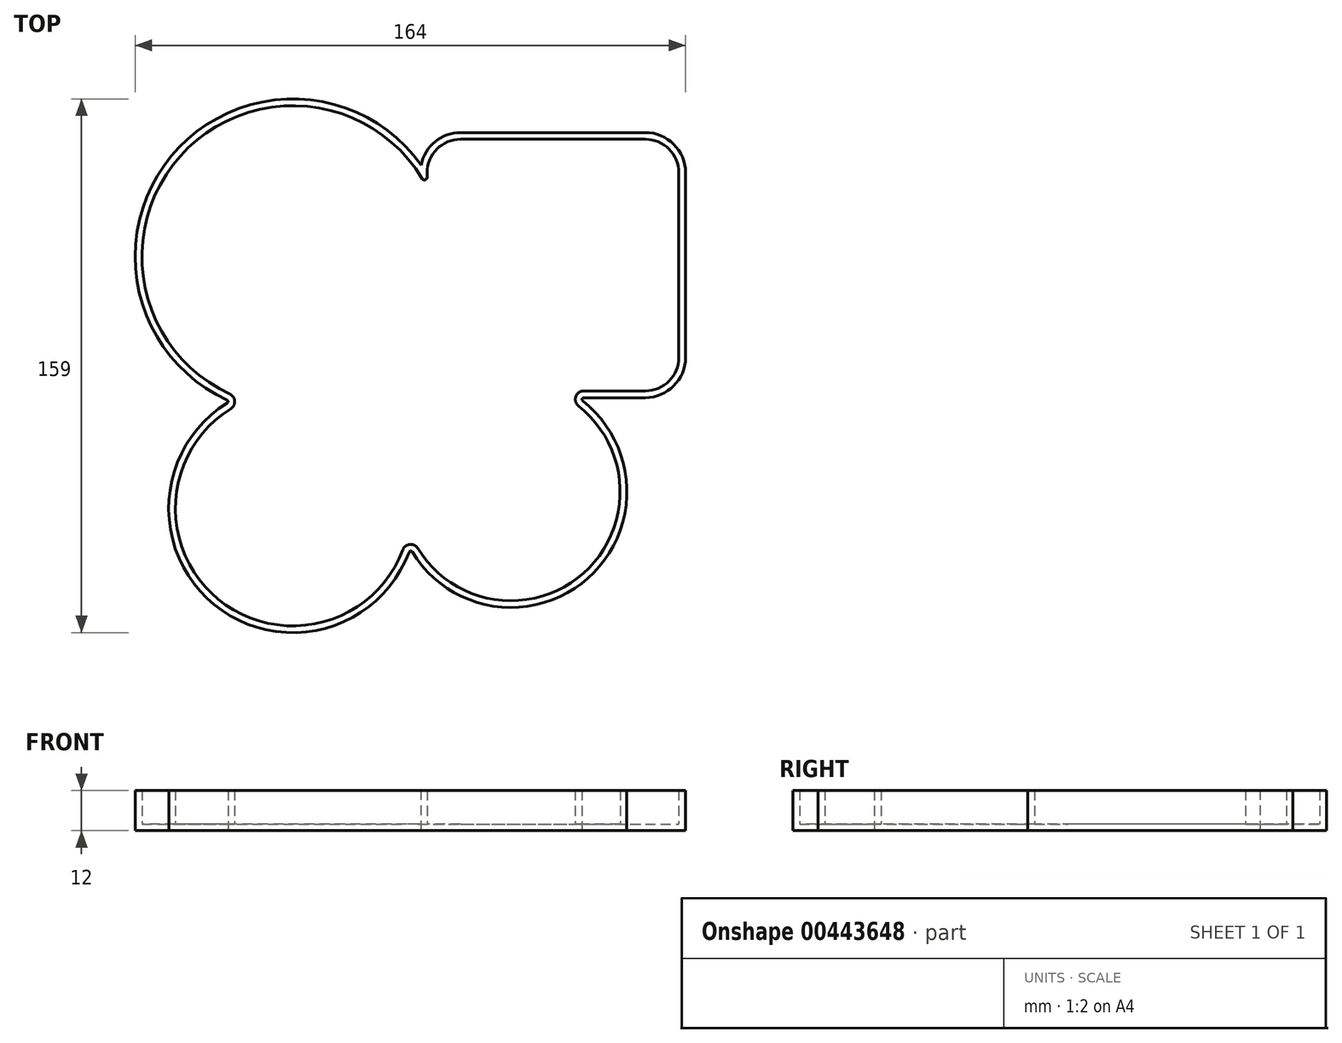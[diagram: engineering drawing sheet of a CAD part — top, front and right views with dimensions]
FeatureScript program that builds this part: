
annotation { "Feature Type Name" : "Feature", "Feature Type Description" : "" }
export const myFeature = defineFeature(function(context is Context, id is Id, definition is map)
    precondition{}
    {
        {
            var Q0;
            Q0=qCreatedBy(makeId("Top.planeOp"),FACE);
            var sketch = newSketch(context, id + "F0", { "sketchPlane" : qUnion([Q0])});
            skArc(sketch, "E0", {"start": v(38.52, 23.27) * mm, "mid": v(-33.57, 29.97) * mm, "end": v(-18.78, -40.9) * mm});
            skArc(sketch, "E1", {"start": v(-18.5, -45.29) * mm, "mid": v(-22.2, -102.07) * mm, "end": v(32.76, -87.32) * mm});
            skArc(sketch, "E2", {"start": v(37.24, -86.9) * mm, "mid": v(86.56, -94.32) * mm, "end": v(85.1, -44.46) * mm});
            skLineSegment(sketch, "E3.bottom", {"start": v(50, 35) * mm, "end": v(105, 35) * mm});
            skLineSegment(sketch, "E3.top", {"start": v(86.65, -40) * mm, "end": v(105, -40) * mm});
            skLineSegment(sketch, "E3.left", {"start": v(40, 25) * mm, "end": v(40, 23.68) * mm});
            skLineSegment(sketch, "E3.right", {"start": v(115, 25) * mm, "end": v(115, -30) * mm});
            skPoint(sketch, "E4.visualSharp", {"position": v(115, 35) * mm});
            skArc(sketch, "E4.filletArc", {"start": v(115, 25) * mm, "mid": v(112.07, 32.07) * mm, "end": v(105, 35) * mm});
            skPoint(sketch, "E5.visualSharp", {"position": v(115, -40) * mm});
            skArc(sketch, "E5.filletArc", {"start": v(105, -40) * mm, "mid": v(112.07, -37.07) * mm, "end": v(115, -30) * mm});
            skPoint(sketch, "E6.visualSharp", {"position": v(40, 35) * mm});
            skArc(sketch, "E6.filletArc", {"start": v(50, 35) * mm, "mid": v(42.93, 32.07) * mm, "end": v(40, 25) * mm});
            skPoint(sketch, "E7.visualSharp", {"position": v(-13.8, -42.83) * mm});
            skArc(sketch, "E7.filletArc", {"start": v(-18.5, -45.29) * mm, "mid": v(-17.33, -43) * mm, "end": v(-18.78, -40.9) * mm});
            skPoint(sketch, "E8.visualSharp", {"position": v(34.46, -81.12) * mm});
            skArc(sketch, "E8.filletArc", {"start": v(37.24, -86.9) * mm, "mid": v(34.87, -85.7) * mm, "end": v(32.76, -87.32) * mm});
            skPoint(sketch, "E9.visualSharp", {"position": v(77.5, -40) * mm});
            skArc(sketch, "E9.filletArc", {"start": v(86.65, -40) * mm, "mid": v(84.29, -41.68) * mm, "end": v(85.1, -44.46) * mm});
            skPoint(sketch, "E10.visualSharp", {"position": v(40, 20.62) * mm});
            skArc(sketch, "E10.filletArc", {"start": v(38.52, 23.27) * mm, "mid": v(39.42, 22.91) * mm, "end": v(40, 23.68) * mm});
            skSolve(sketch);
        }
        {
            var Q0;
            Q0=makeQuery(id+"F0.imprint","IMPRINT",FACE,{"disambiguationData":[TD([[makeQuery(id+"F0.imprint","IMPRINT",EDGE,{"derivedFrom":sQuery(id+"F0.wireOp",EDGE,"E0")}),1.0]])]});
            extrude(context, id + "F1", {"entities" : qUnion([Q0]), "depth" : 10 * mm});
        }
        {
            var Q0;
            Q0=makeQuery(id+"F1.opExtrude","CAP_FACE",FACE,{"disambiguationData":[OSD([sQuery(id+"F0.wireOp",EDGE,"E0"),sQuery(id+"F0.wireOp",EDGE,"E1"),sQuery(id+"F0.wireOp",EDGE,"E2"),sQuery(id+"F0.wireOp",EDGE,"E3.bottom"),sQuery(id+"F0.wireOp",EDGE,"E3.top"),sQuery(id+"F0.wireOp",EDGE,"E3.left"),sQuery(id+"F0.wireOp",EDGE,"E3.right"),sQuery(id+"F0.wireOp",EDGE,"E4.filletArc"),sQuery(id+"F0.wireOp",EDGE,"E5.filletArc"),sQuery(id+"F0.wireOp",EDGE,"E6.filletArc")])],"isStart":false});
            shell(context, id + "F2", {"entities" : qUnion([Q0]), "thickness" : 2 * mm, "oppositeDirection" : true});
        }
    });
